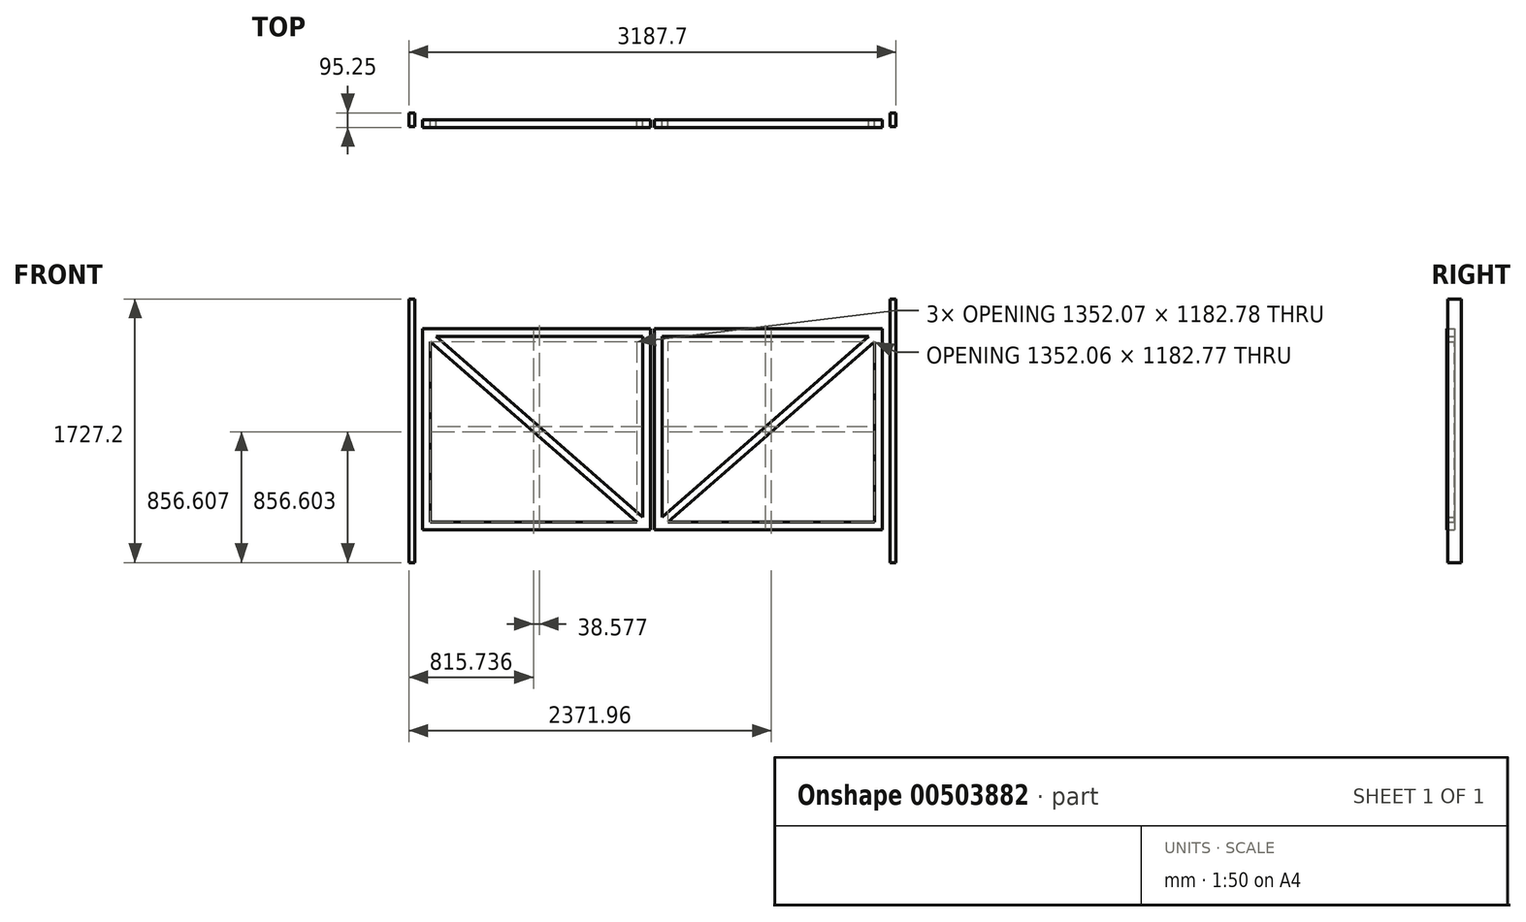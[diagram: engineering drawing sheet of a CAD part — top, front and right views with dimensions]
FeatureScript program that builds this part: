
annotation { "Feature Type Name" : "Feature", "Feature Type Description" : "" }
export const myFeature = defineFeature(function(context is Context, id is Id, definition is map)
    precondition{}
    {
        {
            var Q0;
            Q0=qCreatedBy(makeId("Front.planeOp"),FACE);
            var sketch = newSketch(context, id + "F0", { "sketchPlane" : qUnion([Q0])});
            skLineSegment(sketch, "E0.bottom", {"start": v(-1593.85, 878.22) * mm, "end": v(-1555.75, 878.22) * mm});
            skLineSegment(sketch, "E0.top", {"start": v(-1593.85, -848.98) * mm, "end": v(-1555.75, -848.98) * mm});
            skLineSegment(sketch, "E0.left", {"start": v(-1593.85, 878.22) * mm, "end": v(-1593.85, -848.98) * mm});
            skLineSegment(sketch, "E0.right", {"start": v(-1555.75, 878.22) * mm, "end": v(-1555.75, -848.98) * mm});
            skLineSegment(sketch, "E1.MirrorCS", {"start": v(1593.85, 878.22) * mm, "end": v(1555.75, 878.22) * mm});
            skLineSegment(sketch, "E2.MirrorCS", {"start": v(1593.85, -848.98) * mm, "end": v(1555.75, -848.98) * mm});
            skLineSegment(sketch, "E3.MirrorCS", {"start": v(1555.75, 878.22) * mm, "end": v(1555.75, -848.98) * mm});
            skLineSegment(sketch, "E4.MirrorCS", {"start": v(1593.85, 878.22) * mm, "end": v(1593.85, -848.98) * mm});
            skSolve(sketch);
        }
        {
            var Q0;
            Q0=makeQuery(id+"F0.imprint","IMPRINT",FACE,{"disambiguationData":[TD([[makeQuery(id+"F0.imprint","IMPRINT",EDGE,{"derivedFrom":sQuery(id+"F0.wireOp",EDGE,"E0.bottom")}),-1.0]])]});
            var Q1;
            Q1=makeQuery(id+"F0.imprint","IMPRINT",FACE,{"disambiguationData":[TD([[makeQuery(id+"F0.imprint","IMPRINT",EDGE,{"derivedFrom":sQuery(id+"F0.wireOp",EDGE,"E1.MirrorCS")}),1.0]])]});
            extrude(context, id + "F1", {"entities" : qUnion([Q0, Q1]), "endBound" : BoundingType.SYMMETRIC, "depth" : 88.9 * mm});
        }
        {
            var Q0;
            Q0=qCreatedBy(makeId("Front.planeOp"),FACE);
            var sketch = newSketch(context, id + "F2", { "sketchPlane" : qUnion([Q0])});
            skLineSegment(sketch, "E5.bottom", {"start": v(-1504.95, 878.22) * mm, "end": v(1504.95, 878.22) * mm, "construction": true});
            skLineSegment(sketch, "E5.top", {"start": v(-1504.95, -772.78) * mm, "end": v(1504.95, -772.78) * mm, "construction": true});
            skLineSegment(sketch, "E5.left", {"start": v(-1504.95, 878.22) * mm, "end": v(-1504.95, -772.78) * mm, "construction": true});
            skLineSegment(sketch, "E5.right", {"start": v(1504.95, 878.22) * mm, "end": v(1504.95, -772.78) * mm, "construction": true});
            skLineSegment(sketch, "E6", {"start": v(0, 878.22) * mm, "end": v(0, -772.78) * mm, "construction": true});
            skSolve(sketch);
        }
        {
            var Q0;
            Q0=qCreatedBy(makeId("Front.planeOp"),FACE);
            var sketch = newSketch(context, id + "F3", { "sketchPlane" : qUnion([Q0])});
            skLineSegment(sketch, "E7", {"start": v(-1504.95, 683.57) * mm, "end": v(-12.7, 683.57) * mm});
            skLineSegment(sketch, "E8", {"start": v(-1504.95, 683.57) * mm, "end": v(-1504.95, -634.56) * mm});
            skLineSegment(sketch, "E9", {"start": v(-1504.95, -634.56) * mm, "end": v(-12.7, -634.56) * mm});
            skLineSegment(sketch, "E10", {"start": v(1504.78, -634.56) * mm, "end": v(1504.95, 683.57) * mm});
            skLineSegment(sketch, "E11", {"start": v(12.7, 683.57) * mm, "end": v(1504.95, 683.57) * mm});
            skLineSegment(sketch, "E12", {"start": v(12.7, -634.56) * mm, "end": v(1504.78, -634.56) * mm});
            skLineSegment(sketch, "E13.0", {"start": v(12.7, 683.57) * mm, "end": v(12.7, -634.56) * mm});
            skLineSegment(sketch, "E14.0", {"start": v(-12.7, 683.57) * mm, "end": v(-12.7, -634.56) * mm});
            skLineSegment(sketch, "E15.0", {"start": v(-1454.15, 632.77) * mm, "end": v(-63.5, 632.77) * mm});
            skLineSegment(sketch, "E15.1", {"start": v(-1454.15, 632.77) * mm, "end": v(-1454.15, -583.76) * mm});
            skLineSegment(sketch, "E15.2", {"start": v(-1454.15, -583.76) * mm, "end": v(-63.5, -583.76) * mm});
            skLineSegment(sketch, "E15.3", {"start": v(-63.5, 632.77) * mm, "end": v(-63.5, -583.76) * mm});
            skLineSegment(sketch, "E16.0", {"start": v(63.5, 632.77) * mm, "end": v(1454.14, 632.77) * mm});
            skLineSegment(sketch, "E16.1", {"start": v(63.5, 632.77) * mm, "end": v(63.5, -583.76) * mm});
            skLineSegment(sketch, "E16.2", {"start": v(63.5, -583.76) * mm, "end": v(1453.99, -583.76) * mm});
            skLineSegment(sketch, "E16.3", {"start": v(1453.99, -583.76) * mm, "end": v(1454.14, 632.77) * mm});
            skSolve(sketch);
        }
        {
            var Q0;
            Q0=makeQuery(id+"F3.imprint","IMPRINT",FACE,{"disambiguationData":[TD([[makeQuery(id+"F3.imprint","IMPRINT",EDGE,{"derivedFrom":sQuery(id+"F3.wireOp",EDGE,"E7")}),-1.0]])]});
            var Q1;
            Q1=makeQuery(id+"F3.imprint","IMPRINT",FACE,{"disambiguationData":[TD([[makeQuery(id+"F3.imprint","IMPRINT",EDGE,{"derivedFrom":sQuery(id+"F3.wireOp",EDGE,"E10")}),1.0]])]});
            extrude(context, id + "F4", {"entities" : qUnion([Q0, Q1]), "depth" : 50.8 * mm});
        }
        {
            var Q0;
            Q0=qCreatedBy(makeId("Front.planeOp"),FACE);
            var sketch = newSketch(context, id + "F5", { "sketchPlane" : qUnion([Q0])});
            skLineSegment(sketch, "E17", {"start": v(-1415.57, 632.77) * mm, "end": v(-63.5, -550.02) * mm});
            skLineSegment(sketch, "E18", {"start": v(-1454.15, 599.02) * mm, "end": v(-102.08, -583.76) * mm});
            skLineSegment(sketch, "E19", {"start": v(-63.5, -583.76) * mm, "end": v(-1454.15, 632.77) * mm, "construction": true});
            skLineSegment(sketch, "E20", {"start": v(-1454.15, 599.02) * mm, "end": v(-1454.15, 632.77) * mm});
            skLineSegment(sketch, "E21", {"start": v(-102.08, -583.76) * mm, "end": v(-63.5, -583.76) * mm});
            skLineSegment(sketch, "E22", {"start": v(-63.5, -583.76) * mm, "end": v(-63.5, -550.02) * mm});
            skLineSegment(sketch, "E23", {"start": v(-1454.15, 632.77) * mm, "end": v(-1415.57, 632.77) * mm});
            skSolve(sketch);
        }
        {
            var Q0;
            Q0=makeQuery(id+"F5.imprint","IMPRINT",FACE,{"disambiguationData":[TD([[makeQuery(id+"F5.imprint","IMPRINT",EDGE,{"derivedFrom":sQuery(id+"F5.wireOp",EDGE,"E17")}),-1.0]])]});
            extrude(context, id + "F6", {"entities" : qUnion([Q0]), "depth" : 50.8 * mm});
        }
        {
            var Q0;
            Q0=makeQuery(id+"F6.opExtrude","SWEPT_BODY",BODY,{"disambiguationData":[OSD([sQuery(id+"F5.wireOp",EDGE,"E17"),sQuery(id+"F5.wireOp",EDGE,"E18"),sQuery(id+"F5.wireOp",EDGE,"E20"),sQuery(id+"F5.wireOp",EDGE,"E21"),sQuery(id+"F5.wireOp",EDGE,"E22"),sQuery(id+"F5.wireOp",EDGE,"E23")])]});
            var Q1;
            Q1=qCreatedBy(makeId("Right.planeOp"),FACE);
            mirror(context, id + "F7", {"operationType" : NewBodyOperationType.ADD, "entities" : qUnion([Q0]), "mirrorPlane" : qUnion([Q1])});
        }
    });
